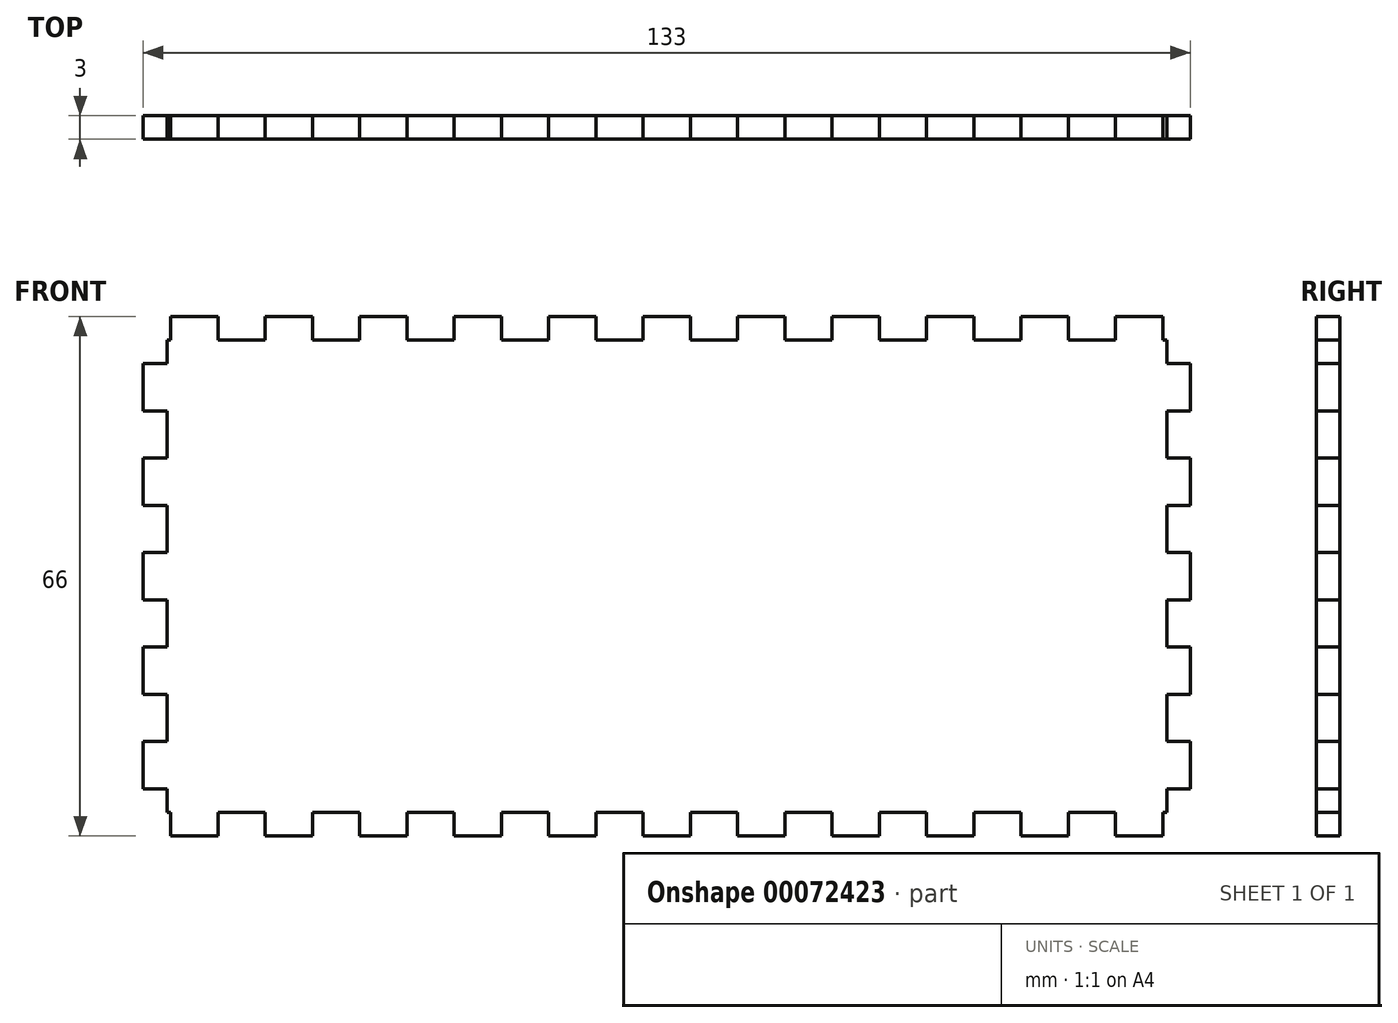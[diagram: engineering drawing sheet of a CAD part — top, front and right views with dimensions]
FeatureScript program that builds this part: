
annotation { "Feature Type Name" : "Feature", "Feature Type Description" : "" }
export const myFeature = defineFeature(function(context is Context, id is Id, definition is map)
    precondition{}
    {
        {
            var Q0;
            Q0=qCreatedBy(makeId("Front.planeOp"),FACE);
            var sketch = newSketch(context, id + "F0", { "sketchPlane" : qUnion([Q0])});
            skLineSegment(sketch, "E0.rect.bottom", {"start": v(63.5, 30) * mm, "end": v(-63.5, 30) * mm});
            skLineSegment(sketch, "E0.rect.top", {"start": v(63.5, -30) * mm, "end": v(-63.5, -30) * mm});
            skLineSegment(sketch, "E0.rect.left", {"start": v(63.5, 30) * mm, "end": v(63.5, -30) * mm});
            skLineSegment(sketch, "E0.rect.right", {"start": v(-63.5, 30) * mm, "end": v(-63.5, -30) * mm});
            skPoint(sketch, "E0.rect.middle", {"position": v(0, 0) * mm});
            skSolve(sketch);
        }
        {
            var Q0;
            Q0 = qSketchRegion(id + "F0", true);
            extrude(context, id + "F1", {"entities" : qUnion([Q0]), "depth" : 3 * mm});
        }
        {
            var Q0;
            Q0=makeQuery(id+"F1.opExtrude","CAP_FACE",FACE,{"disambiguationData":[OSD([sQuery(id+"F0.wireOp",EDGE,"E0.rect.bottom"),sQuery(id+"F0.wireOp",EDGE,"E0.rect.top"),sQuery(id+"F0.wireOp",EDGE,"E0.rect.left"),sQuery(id+"F0.wireOp",EDGE,"E0.rect.right")])],"isStart":false});
            var sketch = newSketch(context, id + "F2", { "sketchPlane" : qUnion([Q0])});
            skPoint(sketch, "E1.start.orphan", {"position": v(0, 30) * mm});
            skLineSegment(sketch, "E2", {"start": v(0, 30) * mm, "end": v(-3, 30) * mm});
            skLineSegment(sketch, "E3", {"start": v(-3, 30) * mm, "end": v(-3, 33) * mm});
            skLineSegment(sketch, "E4", {"start": v(-3, 33) * mm, "end": v(0, 33) * mm});
            skLineSegment(sketch, "E5.MirrorCS", {"start": v(3, 33) * mm, "end": v(0, 33) * mm});
            skLineSegment(sketch, "E6.MirrorCS", {"start": v(3, 30) * mm, "end": v(3, 33) * mm});
            skLineSegment(sketch, "E7.MirrorCS", {"start": v(0, 30) * mm, "end": v(3, 30) * mm});
            skLineSegment(sketch, "E8.1.0.0", {"start": v(12, 30) * mm, "end": v(9, 30) * mm});
            skPoint(sketch, "E8.1.0.1", {"position": v(12, 30) * mm});
            skLineSegment(sketch, "E8.1.0.2", {"start": v(9, 30) * mm, "end": v(9, 33) * mm});
            skLineSegment(sketch, "E8.1.0.3", {"start": v(9, 33) * mm, "end": v(12, 33) * mm});
            skLineSegment(sketch, "E8.1.0.4", {"start": v(15, 33) * mm, "end": v(12, 33) * mm});
            skLineSegment(sketch, "E8.1.0.5", {"start": v(15, 30) * mm, "end": v(15, 33) * mm});
            skLineSegment(sketch, "E8.1.0.6", {"start": v(12, 30) * mm, "end": v(15, 30) * mm});
            skLineSegment(sketch, "E8.2.0.0", {"start": v(24, 30) * mm, "end": v(21, 30) * mm});
            skPoint(sketch, "E8.2.0.1", {"position": v(24, 30) * mm});
            skLineSegment(sketch, "E8.2.0.2", {"start": v(21, 30) * mm, "end": v(21, 33) * mm});
            skLineSegment(sketch, "E8.2.0.3", {"start": v(21, 33) * mm, "end": v(24, 33) * mm});
            skLineSegment(sketch, "E8.2.0.4", {"start": v(27, 33) * mm, "end": v(24, 33) * mm});
            skLineSegment(sketch, "E8.2.0.5", {"start": v(27, 30) * mm, "end": v(27, 33) * mm});
            skLineSegment(sketch, "E8.2.0.6", {"start": v(24, 30) * mm, "end": v(27, 30) * mm});
            skLineSegment(sketch, "E8.3.0.0", {"start": v(36, 30) * mm, "end": v(33, 30) * mm});
            skPoint(sketch, "E8.3.0.1", {"position": v(36, 30) * mm});
            skLineSegment(sketch, "E8.3.0.2", {"start": v(33, 30) * mm, "end": v(33, 33) * mm});
            skLineSegment(sketch, "E8.3.0.3", {"start": v(33, 33) * mm, "end": v(36, 33) * mm});
            skLineSegment(sketch, "E8.3.0.4", {"start": v(39, 33) * mm, "end": v(36, 33) * mm});
            skLineSegment(sketch, "E8.3.0.5", {"start": v(39, 30) * mm, "end": v(39, 33) * mm});
            skLineSegment(sketch, "E8.3.0.6", {"start": v(36, 30) * mm, "end": v(39, 30) * mm});
            skLineSegment(sketch, "E8.4.0.0", {"start": v(48, 30) * mm, "end": v(45, 30) * mm});
            skPoint(sketch, "E8.4.0.1", {"position": v(48, 30) * mm});
            skLineSegment(sketch, "E8.4.0.2", {"start": v(45, 30) * mm, "end": v(45, 33) * mm});
            skLineSegment(sketch, "E8.4.0.3", {"start": v(45, 33) * mm, "end": v(48, 33) * mm});
            skLineSegment(sketch, "E8.4.0.4", {"start": v(51, 33) * mm, "end": v(48, 33) * mm});
            skLineSegment(sketch, "E8.4.0.5", {"start": v(51, 30) * mm, "end": v(51, 33) * mm});
            skLineSegment(sketch, "E8.4.0.6", {"start": v(48, 30) * mm, "end": v(51, 30) * mm});
            skLineSegment(sketch, "E8.5.0.0", {"start": v(60, 30) * mm, "end": v(57, 30) * mm});
            skPoint(sketch, "E8.5.0.1", {"position": v(60, 30) * mm});
            skLineSegment(sketch, "E8.5.0.2", {"start": v(57, 30) * mm, "end": v(57, 33) * mm});
            skLineSegment(sketch, "E8.5.0.3", {"start": v(57, 33) * mm, "end": v(60, 33) * mm});
            skLineSegment(sketch, "E8.5.0.4", {"start": v(63, 33) * mm, "end": v(60, 33) * mm});
            skLineSegment(sketch, "E8.5.0.5", {"start": v(63, 30) * mm, "end": v(63, 33) * mm});
            skLineSegment(sketch, "E8.5.0.6", {"start": v(60, 30) * mm, "end": v(63, 30) * mm});
            skLineSegment(sketch, "E8.direction1", {"start": v(-3, 30) * mm, "end": v(9, 30) * mm, "construction": true});
            skPoint(sketch, "E9.MirrorP", {"position": v(-36, 30) * mm});
            skLineSegment(sketch, "E10.MirrorCS", {"start": v(-33, 30) * mm, "end": v(-33, 33) * mm});
            skLineSegment(sketch, "E11.MirrorCS", {"start": v(-60, 30) * mm, "end": v(-63, 30) * mm});
            skLineSegment(sketch, "E12.MirrorCS", {"start": v(-45, 33) * mm, "end": v(-48, 33) * mm});
            skLineSegment(sketch, "E13.MirrorCS", {"start": v(-36, 30) * mm, "end": v(-33, 30) * mm});
            skLineSegment(sketch, "E14.MirrorCS", {"start": v(-63, 30) * mm, "end": v(-63, 33) * mm});
            skLineSegment(sketch, "E15.MirrorCS", {"start": v(-39, 30) * mm, "end": v(-39, 33) * mm});
            skLineSegment(sketch, "E16.MirrorCS", {"start": v(-57, 30) * mm, "end": v(-57, 33) * mm});
            skLineSegment(sketch, "E17.MirrorCS", {"start": v(-24, 30) * mm, "end": v(-21, 30) * mm});
            skLineSegment(sketch, "E18.MirrorCS", {"start": v(-45, 30) * mm, "end": v(-45, 33) * mm});
            skLineSegment(sketch, "E19.MirrorCS", {"start": v(-12, 30) * mm, "end": v(-15, 30) * mm});
            skLineSegment(sketch, "E20.MirrorCS", {"start": v(-15, 30) * mm, "end": v(-15, 33) * mm});
            skLineSegment(sketch, "E21.MirrorCS", {"start": v(-15, 33) * mm, "end": v(-12, 33) * mm});
            skLineSegment(sketch, "E22.MirrorCS", {"start": v(-9, 33) * mm, "end": v(-12, 33) * mm});
            skLineSegment(sketch, "E23.MirrorCS", {"start": v(-9, 30) * mm, "end": v(-9, 33) * mm});
            skLineSegment(sketch, "E24.MirrorCS", {"start": v(-12, 30) * mm, "end": v(-9, 30) * mm});
            skLineSegment(sketch, "E25.MirrorCS", {"start": v(-27, 33) * mm, "end": v(-24, 33) * mm});
            skLineSegment(sketch, "E26.MirrorCS", {"start": v(-21, 33) * mm, "end": v(-24, 33) * mm});
            skLineSegment(sketch, "E27.MirrorCS", {"start": v(-21, 30) * mm, "end": v(-21, 33) * mm});
            skPoint(sketch, "E28.MirrorP", {"position": v(-60, 30) * mm});
            skLineSegment(sketch, "E29.MirrorCS", {"start": v(-24, 30) * mm, "end": v(-27, 30) * mm});
            skLineSegment(sketch, "E30.MirrorCS", {"start": v(-63, 33) * mm, "end": v(-60, 33) * mm});
            skPoint(sketch, "E31.MirrorP", {"position": v(-24, 30) * mm});
            skLineSegment(sketch, "E32.MirrorCS", {"start": v(-39, 33) * mm, "end": v(-36, 33) * mm});
            skLineSegment(sketch, "E33.MirrorCS", {"start": v(-60, 30) * mm, "end": v(-57, 30) * mm});
            skLineSegment(sketch, "E34.MirrorCS", {"start": v(-48, 30) * mm, "end": v(-45, 30) * mm});
            skLineSegment(sketch, "E35.MirrorCS", {"start": v(-51, 30) * mm, "end": v(-51, 33) * mm});
            skLineSegment(sketch, "E36.MirrorCS", {"start": v(-33, 33) * mm, "end": v(-36, 33) * mm});
            skLineSegment(sketch, "E37.MirrorCS", {"start": v(-48, 30) * mm, "end": v(-51, 30) * mm});
            skPoint(sketch, "E38.MirrorP", {"position": v(-12, 30) * mm});
            skLineSegment(sketch, "E39.MirrorCS", {"start": v(-57, 33) * mm, "end": v(-60, 33) * mm});
            skLineSegment(sketch, "E40.MirrorCS", {"start": v(-36, 30) * mm, "end": v(-39, 30) * mm});
            skLineSegment(sketch, "E41.MirrorCS", {"start": v(-27, 30) * mm, "end": v(-27, 33) * mm});
            skPoint(sketch, "E42.MirrorP", {"position": v(-48, 30) * mm});
            skLineSegment(sketch, "E43.MirrorCS", {"start": v(-51, 33) * mm, "end": v(-48, 33) * mm});
            skLineSegment(sketch, "E44.MirrorCS", {"start": v(-9, -30) * mm, "end": v(-9, -33) * mm});
            skPoint(sketch, "E45.MirrorP", {"position": v(-60, -30) * mm});
            skPoint(sketch, "E46.MirrorP", {"position": v(48, -30) * mm});
            skLineSegment(sketch, "E47.MirrorCS", {"start": v(-12, -30) * mm, "end": v(-9, -30) * mm});
            skLineSegment(sketch, "E48.MirrorCS", {"start": v(33, -30) * mm, "end": v(33, -33) * mm});
            skLineSegment(sketch, "E49.MirrorCS", {"start": v(60, -30) * mm, "end": v(63, -30) * mm});
            skLineSegment(sketch, "E50.MirrorCS", {"start": v(45, -33) * mm, "end": v(48, -33) * mm});
            skLineSegment(sketch, "E51.MirrorCS", {"start": v(-39, -30) * mm, "end": v(-39, -33) * mm});
            skLineSegment(sketch, "E52.MirrorCS", {"start": v(-60, -30) * mm, "end": v(-57, -30) * mm});
            skPoint(sketch, "E53.MirrorP", {"position": v(36, -30) * mm});
            skLineSegment(sketch, "E54.MirrorCS", {"start": v(-51, -33) * mm, "end": v(-48, -33) * mm});
            skLineSegment(sketch, "E55.MirrorCS", {"start": v(36, -30) * mm, "end": v(33, -30) * mm});
            skLineSegment(sketch, "E56.MirrorCS", {"start": v(63, -30) * mm, "end": v(63, -33) * mm});
            skLineSegment(sketch, "E57.MirrorCS", {"start": v(24, -30) * mm, "end": v(21, -30) * mm});
            skLineSegment(sketch, "E58.MirrorCS", {"start": v(45, -30) * mm, "end": v(45, -33) * mm});
            skLineSegment(sketch, "E59.MirrorCS", {"start": v(-63, -30) * mm, "end": v(-63, -33) * mm});
            skLineSegment(sketch, "E60.MirrorCS", {"start": v(-39, -33) * mm, "end": v(-36, -33) * mm});
            skLineSegment(sketch, "E61.MirrorCS", {"start": v(12, -30) * mm, "end": v(15, -30) * mm});
            skLineSegment(sketch, "E62.MirrorCS", {"start": v(15, -30) * mm, "end": v(15, -33) * mm});
            skLineSegment(sketch, "E63.MirrorCS", {"start": v(15, -33) * mm, "end": v(12, -33) * mm});
            skLineSegment(sketch, "E64.MirrorCS", {"start": v(9, -33) * mm, "end": v(12, -33) * mm});
            skLineSegment(sketch, "E65.MirrorCS", {"start": v(9, -30) * mm, "end": v(9, -33) * mm});
            skLineSegment(sketch, "E66.MirrorCS", {"start": v(12, -30) * mm, "end": v(9, -30) * mm});
            skLineSegment(sketch, "E67.MirrorCS", {"start": v(0, -30) * mm, "end": v(3, -30) * mm});
            skLineSegment(sketch, "E68.MirrorCS", {"start": v(3, -30) * mm, "end": v(3, -33) * mm});
            skLineSegment(sketch, "E69.MirrorCS", {"start": v(3, -33) * mm, "end": v(0, -33) * mm});
            skLineSegment(sketch, "E70.MirrorCS", {"start": v(-3, -33) * mm, "end": v(0, -33) * mm});
            skLineSegment(sketch, "E71.MirrorCS", {"start": v(-3, -30) * mm, "end": v(-3, -33) * mm});
            skLineSegment(sketch, "E72.MirrorCS", {"start": v(0, -30) * mm, "end": v(-3, -30) * mm});
            skLineSegment(sketch, "E73.MirrorCS", {"start": v(27, -33) * mm, "end": v(24, -33) * mm});
            skLineSegment(sketch, "E74.MirrorCS", {"start": v(21, -33) * mm, "end": v(24, -33) * mm});
            skLineSegment(sketch, "E75.MirrorCS", {"start": v(-48, -30) * mm, "end": v(-45, -30) * mm});
            skLineSegment(sketch, "E76.MirrorCS", {"start": v(-57, -30) * mm, "end": v(-57, -33) * mm});
            skLineSegment(sketch, "E77.MirrorCS", {"start": v(51, -33) * mm, "end": v(48, -33) * mm});
            skLineSegment(sketch, "E78.MirrorCS", {"start": v(-3, -30) * mm, "end": v(9, -30) * mm, "construction": true});
            skLineSegment(sketch, "E79.MirrorCS", {"start": v(48, -30) * mm, "end": v(51, -30) * mm});
            skLineSegment(sketch, "E80.MirrorCS", {"start": v(33, -33) * mm, "end": v(36, -33) * mm});
            skLineSegment(sketch, "E81.MirrorCS", {"start": v(-33, -33) * mm, "end": v(-36, -33) * mm});
            skLineSegment(sketch, "E82.MirrorCS", {"start": v(-45, -30) * mm, "end": v(-45, -33) * mm});
            skLineSegment(sketch, "E83.MirrorCS", {"start": v(-27, -33) * mm, "end": v(-24, -33) * mm});
            skPoint(sketch, "E84.MirrorP", {"position": v(60, -30) * mm});
            skLineSegment(sketch, "E85.MirrorCS", {"start": v(57, -33) * mm, "end": v(60, -33) * mm});
            skPoint(sketch, "E86.MirrorP", {"position": v(-24, -30) * mm});
            skLineSegment(sketch, "E87.MirrorCS", {"start": v(-51, -30) * mm, "end": v(-51, -33) * mm});
            skLineSegment(sketch, "E88.MirrorCS", {"start": v(-24, -30) * mm, "end": v(-21, -30) * mm});
            skLineSegment(sketch, "E89.MirrorCS", {"start": v(51, -30) * mm, "end": v(51, -33) * mm});
            skLineSegment(sketch, "E90.MirrorCS", {"start": v(-33, -30) * mm, "end": v(-33, -33) * mm});
            skLineSegment(sketch, "E91.MirrorCS", {"start": v(60, -30) * mm, "end": v(57, -30) * mm});
            skLineSegment(sketch, "E92.MirrorCS", {"start": v(39, -33) * mm, "end": v(36, -33) * mm});
            skLineSegment(sketch, "E93.MirrorCS", {"start": v(-48, -30) * mm, "end": v(-51, -30) * mm});
            skLineSegment(sketch, "E94.MirrorCS", {"start": v(-12, -30) * mm, "end": v(-15, -30) * mm});
            skLineSegment(sketch, "E95.MirrorCS", {"start": v(-21, -33) * mm, "end": v(-24, -33) * mm});
            skPoint(sketch, "E96.MirrorP", {"position": v(-36, -30) * mm});
            skPoint(sketch, "E97.MirrorP", {"position": v(-12, -30) * mm});
            skPoint(sketch, "E98.MirrorP", {"position": v(0, -30) * mm});
            skLineSegment(sketch, "E99.MirrorCS", {"start": v(-60, -30) * mm, "end": v(-63, -30) * mm});
            skLineSegment(sketch, "E100.MirrorCS", {"start": v(27, -30) * mm, "end": v(27, -33) * mm});
            skLineSegment(sketch, "E101.MirrorCS", {"start": v(57, -30) * mm, "end": v(57, -33) * mm});
            skLineSegment(sketch, "E102.MirrorCS", {"start": v(39, -30) * mm, "end": v(39, -33) * mm});
            skLineSegment(sketch, "E103.MirrorCS", {"start": v(-15, -30) * mm, "end": v(-15, -33) * mm});
            skLineSegment(sketch, "E104.MirrorCS", {"start": v(-57, -33) * mm, "end": v(-60, -33) * mm});
            skLineSegment(sketch, "E105.MirrorCS", {"start": v(-21, -30) * mm, "end": v(-21, -33) * mm});
            skPoint(sketch, "E106.MirrorP", {"position": v(24, -30) * mm});
            skLineSegment(sketch, "E107.MirrorCS", {"start": v(-36, -30) * mm, "end": v(-33, -30) * mm});
            skLineSegment(sketch, "E108.MirrorCS", {"start": v(-63, -33) * mm, "end": v(-60, -33) * mm});
            skLineSegment(sketch, "E109.MirrorCS", {"start": v(48, -30) * mm, "end": v(45, -30) * mm});
            skLineSegment(sketch, "E110.MirrorCS", {"start": v(-36, -30) * mm, "end": v(-39, -30) * mm});
            skLineSegment(sketch, "E111.MirrorCS", {"start": v(63, -33) * mm, "end": v(60, -33) * mm});
            skLineSegment(sketch, "E112.MirrorCS", {"start": v(24, -30) * mm, "end": v(27, -30) * mm});
            skLineSegment(sketch, "E113.MirrorCS", {"start": v(-9, -33) * mm, "end": v(-12, -33) * mm});
            skLineSegment(sketch, "E114.MirrorCS", {"start": v(21, -30) * mm, "end": v(21, -33) * mm});
            skLineSegment(sketch, "E115.MirrorCS", {"start": v(-27, -30) * mm, "end": v(-27, -33) * mm});
            skLineSegment(sketch, "E116.MirrorCS", {"start": v(-45, -33) * mm, "end": v(-48, -33) * mm});
            skLineSegment(sketch, "E117.MirrorCS", {"start": v(36, -30) * mm, "end": v(39, -30) * mm});
            skPoint(sketch, "E118.MirrorP", {"position": v(12, -30) * mm});
            skLineSegment(sketch, "E119.MirrorCS", {"start": v(-24, -30) * mm, "end": v(-27, -30) * mm});
            skLineSegment(sketch, "E120.MirrorCS", {"start": v(-15, -33) * mm, "end": v(-12, -33) * mm});
            skPoint(sketch, "E121.MirrorP", {"position": v(-48, -30) * mm});
            skSolve(sketch);
        }
        {
            var Q0;
            Q0 = qSketchRegion(id + "F2", true);
            var Q1;
            Q1=makeQuery(id+"F1.opExtrude","CAP_FACE",FACE,{"disambiguationData":[OSD([sQuery(id+"F0.wireOp",EDGE,"E0.rect.bottom"),sQuery(id+"F0.wireOp",EDGE,"E0.rect.top"),sQuery(id+"F0.wireOp",EDGE,"E0.rect.left"),sQuery(id+"F0.wireOp",EDGE,"E0.rect.right")])],"isStart":true});
            extrude(context, id + "F3", {"entities" : qUnion([Q0]), "operationType" : NewBodyOperationType.ADD, "endBound" : BoundingType.UP_TO_SURFACE, "oppositeDirection" : true, "endBoundEntityFace" : qUnion([Q1]), "depth" : 25 * mm});
        }
        {
            var Q0;
            Q0=makeQuery(id+"F1.opExtrude","CAP_FACE",FACE,{"disambiguationData":[OSD([sQuery(id+"F0.wireOp",EDGE,"E0.rect.bottom"),sQuery(id+"F0.wireOp",EDGE,"E0.rect.top"),sQuery(id+"F0.wireOp",EDGE,"E0.rect.left"),sQuery(id+"F0.wireOp",EDGE,"E0.rect.right")])],"isStart":false});
            var sketch = newSketch(context, id + "F4", { "sketchPlane" : qUnion([Q0])});
            skLineSegment(sketch, "E122", {"start": v(-63.5, 0) * mm, "end": v(-63.5, 3) * mm});
            skLineSegment(sketch, "E123", {"start": v(-63.5, 3) * mm, "end": v(-66.5, 3) * mm});
            skLineSegment(sketch, "E124", {"start": v(-66.5, 3) * mm, "end": v(-66.5, 0) * mm});
            skLineSegment(sketch, "E125.MirrorCS", {"start": v(-66.5, -3) * mm, "end": v(-66.5, 0) * mm});
            skLineSegment(sketch, "E126.MirrorCS", {"start": v(-63.5, -3) * mm, "end": v(-66.5, -3) * mm});
            skLineSegment(sketch, "E127.MirrorCS", {"start": v(-63.5, 0) * mm, "end": v(-63.5, -3) * mm});
            skLineSegment(sketch, "E128.0.1.0", {"start": v(-63.5, 12) * mm, "end": v(-63.5, 15) * mm});
            skLineSegment(sketch, "E128.0.1.1", {"start": v(-63.5, 15) * mm, "end": v(-66.5, 15) * mm});
            skLineSegment(sketch, "E128.0.1.2", {"start": v(-63.5, 12) * mm, "end": v(-63.5, 9) * mm});
            skLineSegment(sketch, "E128.0.1.4", {"start": v(-63.5, 9) * mm, "end": v(-66.5, 9) * mm});
            skLineSegment(sketch, "E128.0.1.5", {"start": v(-66.5, 9) * mm, "end": v(-66.5, 12) * mm});
            skLineSegment(sketch, "E128.0.1.6", {"start": v(-66.5, 15) * mm, "end": v(-66.5, 12) * mm});
            skLineSegment(sketch, "E128.0.2.0", {"start": v(-63.5, 24) * mm, "end": v(-63.5, 27) * mm});
            skLineSegment(sketch, "E128.0.2.1", {"start": v(-63.5, 27) * mm, "end": v(-66.5, 27) * mm});
            skLineSegment(sketch, "E128.0.2.2", {"start": v(-63.5, 24) * mm, "end": v(-63.5, 21) * mm});
            skLineSegment(sketch, "E128.0.2.4", {"start": v(-63.5, 21) * mm, "end": v(-66.5, 21) * mm});
            skLineSegment(sketch, "E128.0.2.5", {"start": v(-66.5, 21) * mm, "end": v(-66.5, 24) * mm});
            skLineSegment(sketch, "E128.0.2.6", {"start": v(-66.5, 27) * mm, "end": v(-66.5, 24) * mm});
            skLineSegment(sketch, "E128.direction1", {"start": v(-63.5, 0) * mm, "end": v(-38.5, 0) * mm, "construction": true});
            skLineSegment(sketch, "E128.direction2", {"start": v(-63.5, 0) * mm, "end": v(-63.5, 12) * mm, "construction": true});
            skPoint(sketch, "E129.MirrorCS.end.orphan", {"position": v(-60.5, 3) * mm});
            skPoint(sketch, "E129.MirrorCS.start.orphan", {"position": v(-63.5, 3) * mm});
            skLineSegment(sketch, "E130.MirrorCS", {"start": v(-63.5, -21) * mm, "end": v(-66.5, -21) * mm});
            skLineSegment(sketch, "E131.MirrorCS", {"start": v(-63.5, -12) * mm, "end": v(-63.5, -15) * mm});
            skLineSegment(sketch, "E132.MirrorCS", {"start": v(-63.5, -15) * mm, "end": v(-66.5, -15) * mm});
            skLineSegment(sketch, "E133.MirrorCS", {"start": v(-63.5, -9) * mm, "end": v(-66.5, -9) * mm});
            skLineSegment(sketch, "E134.MirrorCS", {"start": v(-66.5, -27) * mm, "end": v(-66.5, -24) * mm});
            skLineSegment(sketch, "E135.MirrorCS", {"start": v(-66.5, -9) * mm, "end": v(-66.5, -12) * mm});
            skLineSegment(sketch, "E136.MirrorCS", {"start": v(-66.5, -15) * mm, "end": v(-66.5, -12) * mm});
            skLineSegment(sketch, "E137.MirrorCS", {"start": v(-63.5, -24) * mm, "end": v(-63.5, -21) * mm});
            skLineSegment(sketch, "E138.MirrorCS", {"start": v(-66.5, -21) * mm, "end": v(-66.5, -24) * mm});
            skLineSegment(sketch, "E139.MirrorCS", {"start": v(-63.5, -27) * mm, "end": v(-66.5, -27) * mm});
            skLineSegment(sketch, "E140.MirrorCS", {"start": v(-63.5, -12) * mm, "end": v(-63.5, -9) * mm});
            skLineSegment(sketch, "E141.MirrorCS", {"start": v(-63.5, -24) * mm, "end": v(-63.5, -27) * mm});
            skLineSegment(sketch, "E142.MirrorCS", {"start": v(66.5, 27) * mm, "end": v(66.5, 24) * mm});
            skLineSegment(sketch, "E143.MirrorCS", {"start": v(63.5, -12) * mm, "end": v(63.5, -15) * mm});
            skLineSegment(sketch, "E144.MirrorCS", {"start": v(63.5, -12) * mm, "end": v(63.5, -9) * mm});
            skLineSegment(sketch, "E145.MirrorCS", {"start": v(63.5, -27) * mm, "end": v(66.5, -27) * mm});
            skLineSegment(sketch, "E146.MirrorCS", {"start": v(66.5, 15) * mm, "end": v(66.5, 12) * mm});
            skLineSegment(sketch, "E147.MirrorCS", {"start": v(63.5, 24) * mm, "end": v(63.5, 27) * mm});
            skLineSegment(sketch, "E148.MirrorCS", {"start": v(63.5, -21) * mm, "end": v(66.5, -21) * mm});
            skLineSegment(sketch, "E149.MirrorCS", {"start": v(66.5, -21) * mm, "end": v(66.5, -24) * mm});
            skLineSegment(sketch, "E150.MirrorCS", {"start": v(66.5, -27) * mm, "end": v(66.5, -24) * mm});
            skPoint(sketch, "E151.MirrorP", {"position": v(63.5, 3) * mm});
            skLineSegment(sketch, "E152.MirrorCS", {"start": v(63.5, -3) * mm, "end": v(66.5, -3) * mm});
            skLineSegment(sketch, "E153.MirrorCS", {"start": v(66.5, 3) * mm, "end": v(66.5, 0) * mm});
            skLineSegment(sketch, "E154.MirrorCS", {"start": v(63.5, 0) * mm, "end": v(63.5, 3) * mm});
            skLineSegment(sketch, "E155.MirrorCS", {"start": v(63.5, 12) * mm, "end": v(63.5, 9) * mm});
            skLineSegment(sketch, "E156.MirrorCS", {"start": v(63.5, 24) * mm, "end": v(63.5, 21) * mm});
            skLineSegment(sketch, "E157.MirrorCS", {"start": v(63.5, 27) * mm, "end": v(66.5, 27) * mm});
            skLineSegment(sketch, "E158.MirrorCS", {"start": v(66.5, -15) * mm, "end": v(66.5, -12) * mm});
            skLineSegment(sketch, "E159.MirrorCS", {"start": v(63.5, -15) * mm, "end": v(66.5, -15) * mm});
            skLineSegment(sketch, "E160.MirrorCS", {"start": v(63.5, -24) * mm, "end": v(63.5, -27) * mm});
            skLineSegment(sketch, "E161.MirrorCS", {"start": v(63.5, -9) * mm, "end": v(66.5, -9) * mm});
            skLineSegment(sketch, "E162.MirrorCS", {"start": v(63.5, 12) * mm, "end": v(63.5, 15) * mm});
            skLineSegment(sketch, "E163.MirrorCS", {"start": v(63.5, -24) * mm, "end": v(63.5, -21) * mm});
            skLineSegment(sketch, "E164.MirrorCS", {"start": v(66.5, -3) * mm, "end": v(66.5, 0) * mm});
            skLineSegment(sketch, "E165.MirrorCS", {"start": v(63.5, 0) * mm, "end": v(63.5, 12) * mm, "construction": true});
            skLineSegment(sketch, "E166.MirrorCS", {"start": v(66.5, 9) * mm, "end": v(66.5, 12) * mm});
            skLineSegment(sketch, "E167.MirrorCS", {"start": v(63.5, 3) * mm, "end": v(66.5, 3) * mm});
            skLineSegment(sketch, "E168.MirrorCS", {"start": v(63.5, 21) * mm, "end": v(66.5, 21) * mm});
            skLineSegment(sketch, "E169.MirrorCS", {"start": v(63.5, 9) * mm, "end": v(66.5, 9) * mm});
            skLineSegment(sketch, "E170.MirrorCS", {"start": v(66.5, 21) * mm, "end": v(66.5, 24) * mm});
            skLineSegment(sketch, "E171.MirrorCS", {"start": v(63.5, 0) * mm, "end": v(63.5, -3) * mm});
            skLineSegment(sketch, "E172.MirrorCS", {"start": v(66.5, -9) * mm, "end": v(66.5, -12) * mm});
            skLineSegment(sketch, "E173.MirrorCS", {"start": v(63.5, 15) * mm, "end": v(66.5, 15) * mm});
            skSolve(sketch);
        }
        {
            var Q0;
            Q0 = qSketchRegion(id + "F4", true);
            var Q1;
            Q1=makeQuery(id+"F1.opExtrude","CAP_FACE",FACE,{"disambiguationData":[OSD([sQuery(id+"F0.wireOp",EDGE,"E0.rect.bottom"),sQuery(id+"F0.wireOp",EDGE,"E0.rect.top"),sQuery(id+"F0.wireOp",EDGE,"E0.rect.left"),sQuery(id+"F0.wireOp",EDGE,"E0.rect.right")])],"isStart":true});
            extrude(context, id + "F5", {"entities" : qUnion([Q0]), "operationType" : NewBodyOperationType.ADD, "endBound" : BoundingType.UP_TO_SURFACE, "oppositeDirection" : true, "endBoundEntityFace" : qUnion([Q1]), "depth" : 25 * mm});
        }
    });
